# Revit family: SHR1400-SER1300
name_source: partatom
category: Mechanical Equipment
revit_build: Autodesk Revit 2016 (Build: 20170117_1200(x64)
units: mm (PartAtom-declared; Revit-internal decimal feet)

## family parameters
Always vertical = Yes
Cut with Voids When Loaded = No
OmniClass Number = 23.75.00.00
OmniClass Title = Climate Control (HVAC)
Part Type = Normal
Room Calculation Point = No
Round Connector Dimension = Use Diameter
Shared = No
Work Plane-Based = No

## types (3) — shared parameters
Load Classification = HVAC
Manufacturer = Fantech
Number of poles = 1
Power Factor = 1
URL = http://www.fantech.net
Voltage = 120 V
Width = 610 mm  [stored 2.00131 ft]

## per-type parameters (varying)
| type | Apparent Load | Average Airflow | BPM | Current | Description | Model | Not bpm | Product number | Weight | construction |
| SER 1300 | 1300 W | 1300 CFM | No | 10.8 A | Light Commercial Energy Recovery Ventilators | SER 1300 | Yes | 99278 | 208 lbs | 0 |
| SHR 1400 | 1272 W | 1428 CFM | No | 10.6 A | Commercial Heat Recovery Ventilators | SHR 1400 | Yes | 99274 | 236 lbs | 0 |
| SHR 1400 BPM | 1272 W | 1428 CFM | Yes | 10.6 A | Commercial Heat Recovery Ventilators | SHR 1400 | No | 99274, 99302 | 236 lbs | 99 |

note: [stored X ft] marks values corroborated as IEEE doubles in the binary element streams (Revit-internal decimal feet)

## geometry (parser evidence)
native form markers: Blend x2, Sweep x3
no freeform markers — native parametric forms only
